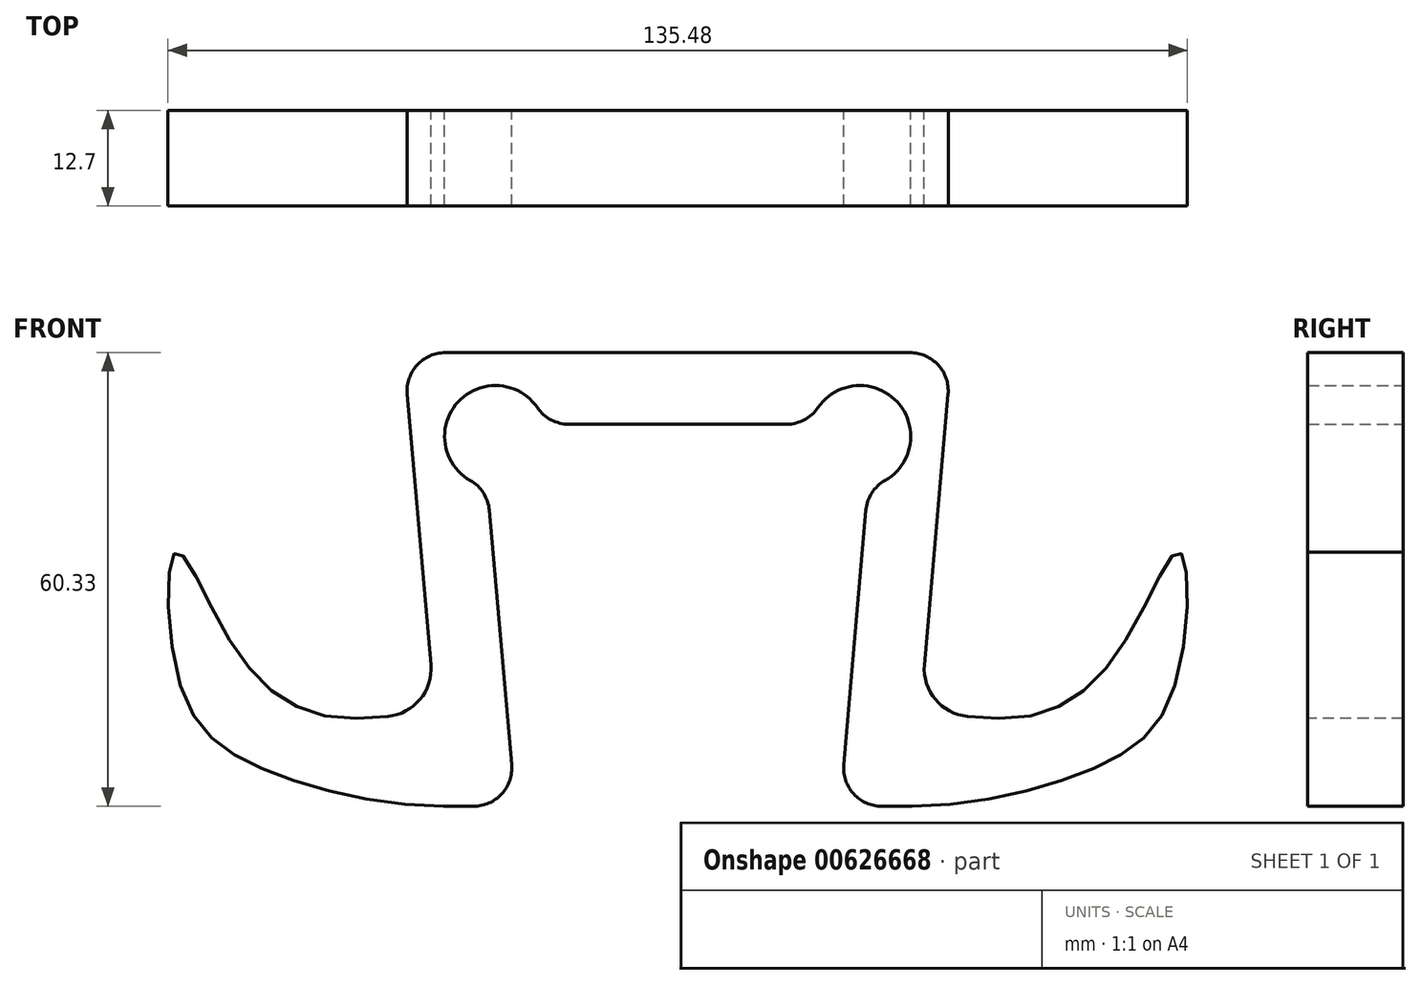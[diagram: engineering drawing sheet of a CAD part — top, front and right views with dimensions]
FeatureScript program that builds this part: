
annotation { "Feature Type Name" : "Feature", "Feature Type Description" : "" }
export const myFeature = defineFeature(function(context is Context, id is Id, definition is map)
    precondition{}
    {
        {
            var Q0;
            Q0=qCreatedBy(makeId("Front.planeOp"),FACE);
            var sketch = newSketch(context, id + "F0", { "sketchPlane" : qUnion([Q0])});
            skLineSegment(sketch, "E0.MirrorCS", {"start": v(0, 9.53) * mm, "end": v(36.43, 9.52) * mm});
            skLineSegment(sketch, "E1.MirrorCS", {"start": v(0, 0) * mm, "end": v(17.66, 0) * mm});
            skLineSegment(sketch, "E2.MirrorCS", {"start": v(25.3, -8.28) * mm, "end": v(22.07, -45.28) * mm});
            skLineSegment(sketch, "E3.MirrorCS", {"start": v(36.43, 9.52) * mm, "end": v(32.8, -31.97) * mm});
            skLineSegment(sketch, "E4.MirrorCS", {"start": v(31.15, -50.8) * mm, "end": v(27.13, -50.8) * mm});
            skFitSpline(sketch, "E5", {"points": [v(32.24, -38.32) * mm, v(46.8, -38.78) * mm, v(59.85, -28.24) * mm, v(66.72, -17.02) * mm, v(66.02, -34.95) * mm, v(55.37, -45.72) * mm, v(31.15, -50.8) * mm], "startDerivative": vector(59.08, 1.63) * mm, "endDerivative": vector(-124.09, 0) * mm});
            skArc(sketch, "E6.filletArc", {"start": v(32.8, -31.97) * mm, "mid": v(34.25, -36.59) * mm, "end": v(38.53, -38.85) * mm});
            skPoint(sketch, "E7.visualSharp", {"position": v(21.59, -50.8) * mm});
            skArc(sketch, "E7.filletArc", {"start": v(22.07, -45.28) * mm, "mid": v(23.39, -49.15) * mm, "end": v(27.13, -50.8) * mm});
            skArc(sketch, "E8.MirrorCS", {"start": v(17.66, 0) * mm, "mid": v(29.18, 2.97) * mm, "end": v(25.3, -8.28) * mm});
            skPoint(sketch, "E9.orphan", {"position": v(26.03, 0) * mm});
            skLineSegment(sketch, "E10", {"start": v(0, 0) * mm, "end": v(0, 9.53) * mm, "construction": true});
            skLineSegment(sketch, "E11.MirrorCS", {"start": v(-31.15, -50.8) * mm, "end": v(-27.13, -50.8) * mm});
            skPoint(sketch, "E12.MirrorP", {"position": v(-26.03, 0) * mm});
            skArc(sketch, "E13.MirrorCS", {"start": v(-32.8, -31.97) * mm, "mid": v(-34.25, -36.59) * mm, "end": v(-38.53, -38.85) * mm});
            skArc(sketch, "E14.MirrorCS", {"start": v(-22.07, -45.28) * mm, "mid": v(-23.39, -49.15) * mm, "end": v(-27.13, -50.8) * mm});
            skPoint(sketch, "E15.MirrorP", {"position": v(-32.24, -38.32) * mm});
            skLineSegment(sketch, "E16.MirrorCS", {"start": v(-25.3, -8.28) * mm, "end": v(-22.07, -45.28) * mm});
            skLineSegment(sketch, "E17.MirrorCS", {"start": v(0, 0) * mm, "end": v(-17.66, 0) * mm});
            skPoint(sketch, "E18.MirrorP", {"position": v(-21.59, -50.8) * mm});
            skLineSegment(sketch, "E19.MirrorCS", {"start": v(0, 9.53) * mm, "end": v(-36.43, 9.52) * mm});
            skLineSegment(sketch, "E20.MirrorCS", {"start": v(-36.43, 9.52) * mm, "end": v(-32.8, -31.97) * mm});
            skArc(sketch, "E21.MirrorCS", {"start": v(-17.66, 0) * mm, "mid": v(-29.18, 2.97) * mm, "end": v(-25.3, -8.28) * mm});
            skFitSpline(sketch, "E22.MirrorCS", {"points": [v(-32.24, -38.32) * mm, v(-46.8, -38.78) * mm, v(-59.85, -28.24) * mm, v(-66.72, -17.02) * mm, v(-66.02, -34.95) * mm, v(-55.37, -45.72) * mm, v(-31.15, -50.8) * mm], "startDerivative": vector(-59.08, 1.63) * mm, "endDerivative": vector(124.09, 0) * mm});
            skSolve(sketch);
        }
        {
            var Q0;
            Q0 = qSketchRegion(id + "F0", true);
            extrude(context, id + "F1", {"entities" : qUnion([Q0]), "depth" : 12.7 * mm, "offsetDistance" : 25.4 * mm});
        }
        {
            var Q0;
            Q0=makeQuery(id+"F1.opExtrude","SWEPT_EDGE",EDGE,{"disambiguationData":[OSD([sQuery(id+"F0.wireOp",EDGE,"E19.MirrorCS"),sQuery(id+"F0.wireOp",EDGE,"E20.MirrorCS")])]});
            var Q1;
            Q1=makeQuery(id+"F1.opExtrude","SWEPT_EDGE",EDGE,{"disambiguationData":[OSD([sQuery(id+"F0.wireOp",EDGE,"E16.MirrorCS"),sQuery(id+"F0.wireOp",EDGE,"E21.MirrorCS")])]});
            var Q2;
            Q2=makeQuery(id+"F1.opExtrude","SWEPT_EDGE",EDGE,{"disambiguationData":[OSD([sQuery(id+"F0.wireOp",EDGE,"E17.MirrorCS"),sQuery(id+"F0.wireOp",EDGE,"E21.MirrorCS")])]});
            var Q3;
            Q3=makeQuery(id+"F1.opExtrude","SWEPT_EDGE",EDGE,{"disambiguationData":[OSD([sQuery(id+"F0.wireOp",EDGE,"E1.MirrorCS"),sQuery(id+"F0.wireOp",EDGE,"E8.MirrorCS")])]});
            var Q4;
            Q4=makeQuery(id+"F1.opExtrude","SWEPT_EDGE",EDGE,{"disambiguationData":[OSD([sQuery(id+"F0.wireOp",EDGE,"E2.MirrorCS"),sQuery(id+"F0.wireOp",EDGE,"E8.MirrorCS")])]});
            var Q5;
            Q5=makeQuery(id+"F1.opExtrude","SWEPT_EDGE",EDGE,{"disambiguationData":[OSD([sQuery(id+"F0.wireOp",EDGE,"E0.MirrorCS"),sQuery(id+"F0.wireOp",EDGE,"E3.MirrorCS")])]});
            fillet(context, id + "F2", {"entities" : qUnion([Q0, Q1, Q2, Q3, Q4, Q5]), "radius" : 5.08 * mm, "tangentPropagation" : true, "allowEdgeOverflow" : false});
        }
    });
